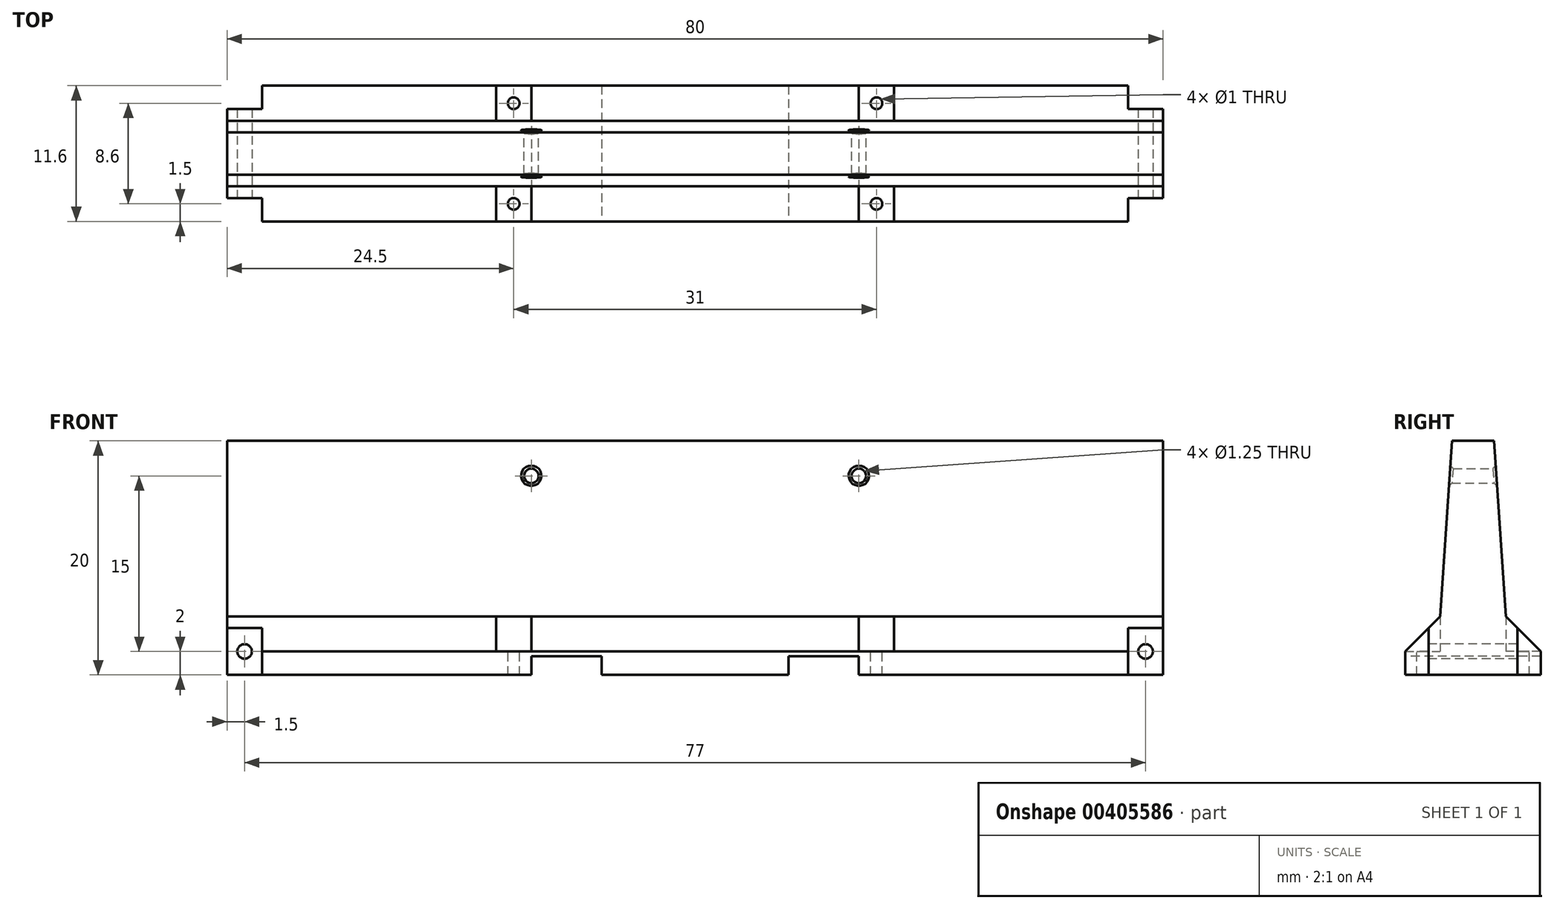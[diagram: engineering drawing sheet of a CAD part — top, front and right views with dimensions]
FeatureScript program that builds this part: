
annotation { "Feature Type Name" : "Feature", "Feature Type Description" : "" }
export const myFeature = defineFeature(function(context is Context, id is Id, definition is map)
    precondition{}
    {
        {
            var Q0;
            Q0=qCreatedBy(makeId("Top.planeOp"),FACE);
            var sketch = newSketch(context, id + "F0", { "sketchPlane" : qUnion([Q0])});
            skLineSegment(sketch, "E0.bottom", {"start": v(0, 0) * mm, "end": v(80, 0) * mm});
            skLineSegment(sketch, "E0.top", {"start": v(0, 11.6) * mm, "end": v(80, 11.6) * mm});
            skLineSegment(sketch, "E0.left", {"start": v(0, 0) * mm, "end": v(0, 11.6) * mm});
            skLineSegment(sketch, "E0.right", {"start": v(80, 0) * mm, "end": v(80, 11.6) * mm});
            skSolve(sketch);
        }
        {
            var Q0;
            Q0 = qSketchRegion(id + "F0", true);
            extrude(context, id + "F1", {"entities" : qUnion([Q0]), "depth" : 2 * mm});
        }
        {
            var Q0;
            Q0=makeQuery(id+"F1.opExtrude","SWEPT_FACE",FACE,{"disambiguationData":[OSD([sQuery(id+"F0.wireOp",EDGE,"E0.bottom")])]});
            var sketch = newSketch(context, id + "F2", { "sketchPlane" : qUnion([Q0])});
            skLineSegment(sketch, "E1", {"start": v(0, 0) * mm, "end": v(26, 0) * mm, "construction": true});
            skLineSegment(sketch, "E2", {"start": v(26, 0) * mm, "end": v(26, 1.6) * mm});
            skLineSegment(sketch, "E3", {"start": v(26, 1.6) * mm, "end": v(32, 1.6) * mm});
            skLineSegment(sketch, "E4", {"start": v(32, 1.6) * mm, "end": v(32, 0) * mm});
            skLineSegment(sketch, "E5", {"start": v(32, 0) * mm, "end": v(48, 0) * mm, "construction": true});
            skLineSegment(sketch, "E6", {"start": v(48, 0) * mm, "end": v(48, 1.6) * mm});
            skLineSegment(sketch, "E7", {"start": v(48, 1.6) * mm, "end": v(54, 1.6) * mm});
            skLineSegment(sketch, "E8", {"start": v(54, 1.6) * mm, "end": v(54, 0) * mm});
            skLineSegment(sketch, "E9", {"start": v(54, 0) * mm, "end": v(48, 0) * mm});
            skLineSegment(sketch, "E10", {"start": v(32, 0) * mm, "end": v(26, 0) * mm});
            skSolve(sketch);
        }
        {
            var Q0;
            Q0=makeQuery(id+"F2.imprint","IMPRINT",FACE,{"disambiguationData":[TD([[makeQuery(id+"F2.imprint","IMPRINT",EDGE,{"derivedFrom":sQuery(id+"F2.wireOp",EDGE,"E2")}),-1.0]])]});
            var Q1;
            Q1=makeQuery(id+"F2.imprint","IMPRINT",FACE,{"disambiguationData":[TD([[makeQuery(id+"F2.imprint","IMPRINT",EDGE,{"derivedFrom":sQuery(id+"F2.wireOp",EDGE,"E6")}),-1.0]])]});
            var Q2;
            Q2=sQuery(id+"F2.wireOp",EDGE,"E1");
            extrude(context, id + "F3", {"entities" : qUnion([Q0, Q1]), "operationType" : NewBodyOperationType.REMOVE, "surfaceEntities" : qUnion([Q2]), "oppositeDirection" : true, "depth" : 25 * mm});
        }
        {
            var Q0;
            Q0=makeQuery(id+"F1.opExtrude","CAP_FACE",FACE,{"disambiguationData":[OSD([sQuery(id+"F0.wireOp",EDGE,"E0.bottom"),sQuery(id+"F0.wireOp",EDGE,"E0.top"),sQuery(id+"F0.wireOp",EDGE,"E0.left"),sQuery(id+"F0.wireOp",EDGE,"E0.right")])],"isStart":false});
            var sketch = newSketch(context, id + "F4", { "sketchPlane" : qUnion([Q0])});
            skLineSegment(sketch, "E11.bottom", {"start": v(0, 11.6) * mm, "end": v(80, 11.6) * mm});
            skLineSegment(sketch, "E11.top", {"start": v(0, 0) * mm, "end": v(80, 0) * mm});
            skLineSegment(sketch, "E11.left", {"start": v(0, 11.6) * mm, "end": v(0, 0) * mm});
            skLineSegment(sketch, "E11.right", {"start": v(80, 11.6) * mm, "end": v(80, 0) * mm});
            skSolve(sketch);
        }
        {
            var Q0;
            Q0 = qSketchRegion(id + "F4", true);
            extrude(context, id + "F5", {"entities" : qUnion([Q0]), "operationType" : NewBodyOperationType.ADD, "depth" : 18 * mm});
        }
        {
            var Q0;
            Q0=makeQuery(id+"F5.boolean.opBoolean","MERGE",FACE,{"derivedFrom":[makeQuery(id+"F1.opExtrude","SWEPT_FACE",FACE,{"disambiguationData":[OSD([sQuery(id+"F0.wireOp",EDGE,"E0.right")])]}),makeQuery(id+"F5.opExtrude","SWEPT_FACE",FACE,{"disambiguationData":[OSD([sQuery(id+"F4.wireOp",EDGE,"E11.right")])]})]});
            var sketch = newSketch(context, id + "F6", { "sketchPlane" : qUnion([Q0])});
            skLineSegment(sketch, "E12", {"start": v(11.6, 0) * mm, "end": v(11.6, 2) * mm, "construction": true});
            skLineSegment(sketch, "E13", {"start": v(11.6, 2) * mm, "end": v(8.6, 5) * mm});
            skLineSegment(sketch, "E14", {"start": v(8.6, 5) * mm, "end": v(7.6, 20) * mm});
            skLineSegment(sketch, "E15", {"start": v(7.6, 20) * mm, "end": v(4, 20) * mm});
            skLineSegment(sketch, "E16", {"start": v(5.8, 0) * mm, "end": v(5.8, 20) * mm, "construction": true});
            skLineSegment(sketch, "E17.MirrorCS", {"start": v(3, 5) * mm, "end": v(4, 20) * mm});
            skLineSegment(sketch, "E18.MirrorCS", {"start": v(0, 2) * mm, "end": v(3, 5) * mm});
            skLineSegment(sketch, "E19", {"start": v(0, 2) * mm, "end": v(0, 0) * mm});
            skLineSegment(sketch, "E20", {"start": v(0, 0) * mm, "end": v(11.6, 0) * mm});
            skSolve(sketch);
        }
        {
            var Q0;
            {var subQ0=sQuery(id+"F6.wireOp",EDGE,"E17.MirrorCS");Q0=makeQuery(id+"F6.imprint","IMPRINT",FACE,{"disambiguationData":[TD([[makeQuery(id+"F6.imprint","IMPRINT",EDGE,{"derivedFrom":subQ0}),1.0]])]});}
            var Q1;
            {var subQ0=sQuery(id+"F6.wireOp",EDGE,"E13");Q1=makeQuery(id+"F6.imprint","IMPRINT",FACE,{"disambiguationData":[TD([[makeQuery(id+"F6.imprint","IMPRINT",EDGE,{"derivedFrom":subQ0}),-1.0]])]});}
            extrude(context, id + "F7", {"entities" : qUnion([Q0, Q1]), "operationType" : NewBodyOperationType.REMOVE, "oppositeDirection" : true, "depth" : 80 * mm});
        }
        {
            var Q0;
            {var subQ0=sQuery(id+"F0.wireOp",EDGE,"E0.bottom");var subQ1=sQuery(id+"F0.wireOp",EDGE,"E0.right");var subQ2=sQuery(id+"F0.wireOp",EDGE,"E0.top");Q0=makeQuery(id+"F3.boolean.opBoolean","SPLIT",FACE,{"disambiguationData":[TD([makeQuery(id+"F1.opExtrude","SWEPT_FACE",FACE,{"disambiguationData":[OSD([subQ1])]})])],"derivedFrom":makeQuery(id+"F1.opExtrude","CAP_FACE",FACE,{"disambiguationData":[OSD([subQ0,subQ2,sQuery(id+"F0.wireOp",EDGE,"E0.left"),subQ1])],"isStart":true})});}
            var sketch = newSketch(context, id + "F8", { "sketchPlane" : qUnion([Q0])});
            skLineSegment(sketch, "E21", {"start": v(0, 0) * mm, "end": v(26, 0) * mm, "construction": true});
            skLineSegment(sketch, "E22.bottom", {"start": v(26, 0) * mm, "end": v(23, 0) * mm});
            skLineSegment(sketch, "E22.top", {"start": v(26, -3) * mm, "end": v(23, -3) * mm});
            skLineSegment(sketch, "E22.left", {"start": v(26, 0) * mm, "end": v(26, -3) * mm});
            skLineSegment(sketch, "E22.right", {"start": v(23, 0) * mm, "end": v(23, -3) * mm});
            skLineSegment(sketch, "E23", {"start": v(0, 0) * mm, "end": v(0, -11.6) * mm, "construction": true});
            skLineSegment(sketch, "E24", {"start": v(0, -5.8) * mm, "end": v(7.98, -5.8) * mm, "construction": true});
            skLineSegment(sketch, "E25.MirrorCS", {"start": v(23, -11.6) * mm, "end": v(23, -8.6) * mm});
            skLineSegment(sketch, "E26.MirrorCS", {"start": v(0, -11.6) * mm, "end": v(26, -11.6) * mm, "construction": true});
            skLineSegment(sketch, "E27.MirrorCS", {"start": v(26, -11.6) * mm, "end": v(26, -8.6) * mm});
            skLineSegment(sketch, "E28.MirrorCS", {"start": v(26, -8.6) * mm, "end": v(23, -8.6) * mm});
            skLineSegment(sketch, "E29.bottom", {"start": v(23, -8.6) * mm, "end": v(26, -8.6) * mm});
            skLineSegment(sketch, "E29.top", {"start": v(23, -11.6) * mm, "end": v(26, -11.6) * mm});
            skLineSegment(sketch, "E29.left", {"start": v(23, -8.6) * mm, "end": v(23, -11.6) * mm});
            skLineSegment(sketch, "E29.right", {"start": v(26, -8.6) * mm, "end": v(26, -11.6) * mm});
            skLineSegment(sketch, "E30", {"start": v(0, 0) * mm, "end": v(40, 0) * mm, "construction": true});
            skLineSegment(sketch, "E31", {"start": v(40, 0) * mm, "end": v(40, -11.6) * mm, "construction": true});
            skLineSegment(sketch, "E32.MirrorCS", {"start": v(54, -3) * mm, "end": v(57, -3) * mm});
            skLineSegment(sketch, "E33.MirrorCS", {"start": v(57, 0) * mm, "end": v(57, -3) * mm});
            skLineSegment(sketch, "E34.MirrorCS", {"start": v(80, 0) * mm, "end": v(54, 0) * mm, "construction": true});
            skLineSegment(sketch, "E35.MirrorCS", {"start": v(54, 0) * mm, "end": v(54, -3) * mm});
            skLineSegment(sketch, "E36.MirrorCS", {"start": v(57, -8.6) * mm, "end": v(54, -8.6) * mm});
            skLineSegment(sketch, "E37.MirrorCS", {"start": v(57, -11.6) * mm, "end": v(57, -8.6) * mm});
            skLineSegment(sketch, "E38.MirrorCS", {"start": v(80, -11.6) * mm, "end": v(54, -11.6) * mm, "construction": true});
            skLineSegment(sketch, "E39.MirrorCS", {"start": v(54, -11.6) * mm, "end": v(54, -8.6) * mm});
            skLineSegment(sketch, "E40.bottom", {"start": v(54, 0) * mm, "end": v(57, 0) * mm});
            skLineSegment(sketch, "E41.bottom", {"start": v(54, -8.6) * mm, "end": v(57, -8.6) * mm});
            skLineSegment(sketch, "E41.top", {"start": v(54, -11.6) * mm, "end": v(57, -11.6) * mm});
            skLineSegment(sketch, "E41.left", {"start": v(54, -8.6) * mm, "end": v(54, -11.6) * mm});
            skLineSegment(sketch, "E41.right", {"start": v(57, -8.6) * mm, "end": v(57, -11.6) * mm});
            skSolve(sketch);
        }
        {
            var Q0;
            Q0 = qSketchRegion(id + "F8", true);
            extrude(context, id + "F9", {"entities" : qUnion([Q0]), "operationType" : NewBodyOperationType.REMOVE, "oppositeDirection" : true, "depth" : 25 * mm, "hasSecondDirection" : true, "secondDirectionOppositeDirection" : true, "secondDirectionDepth" : 2 * mm});
        }
        {
            var Q0;
            Q0=makeQuery(id+"F9.boolean.opBoolean","COPY",FACE,{"derivedFrom":makeQuery(id+"F9.opExtrude","CAP_FACE",FACE,{"disambiguationData":[OSD([sQuery(id+"F8.wireOp",EDGE,"E22.bottom"),sQuery(id+"F8.wireOp",EDGE,"E22.top"),sQuery(id+"F8.wireOp",EDGE,"E22.left"),sQuery(id+"F8.wireOp",EDGE,"E22.right")])],"isStart":true})});
            var sketch = newSketch(context, id + "F10", { "sketchPlane" : qUnion([Q0])});
            skCircle(sketch, "E42", {"center": v(24.5, 1.5) * mm, "radius": 0.5 * mm});
            skPoint(sketch, "E42.centerSnap0", {"position": v(24.5, 3) * mm});
            skPoint(sketch, "E42.centerSnap1", {"position": v(26, 1.5) * mm});
            skSolve(sketch);
        }
        {
            var Q0;
            Q0 = qSketchRegion(id + "F10", true);
            extrude(context, id + "F11", {"entities" : qUnion([Q0]), "operationType" : NewBodyOperationType.REMOVE, "oppositeDirection" : true, "depth" : 25 * mm});
        }
        {
            var Q0;
            Q0=makeQuery(id+"F9.boolean.opBoolean","COPY",FACE,{"derivedFrom":makeQuery(id+"F9.opExtrude","CAP_FACE",FACE,{"disambiguationData":[OSD([sQuery(id+"F8.wireOp",EDGE,"E29.bottom"),sQuery(id+"F8.wireOp",EDGE,"E29.top"),sQuery(id+"F8.wireOp",EDGE,"E29.left"),sQuery(id+"F8.wireOp",EDGE,"E29.right")])],"isStart":true})});
            var sketch = newSketch(context, id + "F12", { "sketchPlane" : qUnion([Q0])});
            skCircle(sketch, "E43", {"center": v(24.5, 10.1) * mm, "radius": 0.5 * mm});
            skPoint(sketch, "E43.centerSnap0", {"position": v(23, 10.1) * mm});
            skPoint(sketch, "E43.centerSnap1", {"position": v(24.5, 11.6) * mm});
            skSolve(sketch);
        }
        {
            var Q0;
            Q0 = qSketchRegion(id + "F12", true);
            extrude(context, id + "F13", {"entities" : qUnion([Q0]), "operationType" : NewBodyOperationType.REMOVE, "oppositeDirection" : true, "depth" : 25 * mm});
        }
        {
            var Q0;
            Q0=makeQuery(id+"F9.boolean.opBoolean","COPY",FACE,{"derivedFrom":makeQuery(id+"F9.opExtrude","CAP_FACE",FACE,{"disambiguationData":[OSD([sQuery(id+"F8.wireOp",EDGE,"E41.bottom"),sQuery(id+"F8.wireOp",EDGE,"E41.top"),sQuery(id+"F8.wireOp",EDGE,"E41.left"),sQuery(id+"F8.wireOp",EDGE,"E41.right")])],"isStart":true})});
            var sketch = newSketch(context, id + "F14", { "sketchPlane" : qUnion([Q0])});
            skCircle(sketch, "E44", {"center": v(55.5, 10.1) * mm, "radius": 0.5 * mm});
            skPoint(sketch, "E44.centerSnap0", {"position": v(54, 10.1) * mm});
            skPoint(sketch, "E44.centerSnap1", {"position": v(55.5, 11.6) * mm});
            skSolve(sketch);
        }
        {
            var Q0;
            Q0 = qSketchRegion(id + "F14", true);
            extrude(context, id + "F15", {"entities" : qUnion([Q0]), "operationType" : NewBodyOperationType.REMOVE, "oppositeDirection" : true, "depth" : 25 * mm});
        }
        {
            var Q0;
            Q0=makeQuery(id+"F9.boolean.opBoolean","COPY",FACE,{"derivedFrom":makeQuery(id+"F9.opExtrude","CAP_FACE",FACE,{"disambiguationData":[OSD([sQuery(id+"F8.wireOp",EDGE,"E40.bottom"),sQuery(id+"F8.wireOp",EDGE,"E32.MirrorCS"),sQuery(id+"F8.wireOp",EDGE,"E35.MirrorCS"),sQuery(id+"F8.wireOp",EDGE,"E33.MirrorCS")])],"isStart":true})});
            var sketch = newSketch(context, id + "F16", { "sketchPlane" : qUnion([Q0])});
            skCircle(sketch, "E45", {"center": v(55.5, 1.5) * mm, "radius": 0.5 * mm});
            skPoint(sketch, "E45.centerSnap0", {"position": v(54, 1.5) * mm});
            skPoint(sketch, "E45.centerSnap1", {"position": v(55.5, 0) * mm});
            skSolve(sketch);
        }
        {
            var Q0;
            Q0 = qSketchRegion(id + "F16", true);
            extrude(context, id + "F17", {"entities" : qUnion([Q0]), "operationType" : NewBodyOperationType.REMOVE, "oppositeDirection" : true, "depth" : 25 * mm});
        }
        {
            var Q0;
            Q0=makeQuery(id+"F5.boolean.opBoolean","MERGE",FACE,{"derivedFrom":[makeQuery(id+"F1.opExtrude","SWEPT_FACE",FACE,{"disambiguationData":[OSD([sQuery(id+"F0.wireOp",EDGE,"E0.bottom")])]}),makeQuery(id+"F5.opExtrude","SWEPT_FACE",FACE,{"disambiguationData":[OSD([sQuery(id+"F4.wireOp",EDGE,"E11.top")])]})]});
            var sketch = newSketch(context, id + "F18", { "sketchPlane" : qUnion([Q0])});
            skLineSegment(sketch, "E46.bottom", {"start": v(0, 0) * mm, "end": v(3, 0) * mm});
            skLineSegment(sketch, "E46.top", {"start": v(0, 5) * mm, "end": v(3, 5) * mm});
            skLineSegment(sketch, "E46.left", {"start": v(0, 0) * mm, "end": v(0, 5) * mm});
            skLineSegment(sketch, "E46.right", {"start": v(3, 0) * mm, "end": v(3, 5) * mm});
            skLineSegment(sketch, "E47.bottom", {"start": v(80, 0) * mm, "end": v(77, 0) * mm});
            skLineSegment(sketch, "E47.top", {"start": v(80, 5) * mm, "end": v(77, 5) * mm});
            skLineSegment(sketch, "E47.left", {"start": v(80, 0) * mm, "end": v(80, 5) * mm});
            skLineSegment(sketch, "E47.right", {"start": v(77, 0) * mm, "end": v(77, 5) * mm});
            skSolve(sketch);
        }
        {
            var Q0;
            Q0 = qSketchRegion(id + "F18", true);
            extrude(context, id + "F19", {"entities" : qUnion([Q0]), "operationType" : NewBodyOperationType.REMOVE, "oppositeDirection" : true, "depth" : 2 * mm});
        }
        {
            var Q0;
            Q0=makeQuery(id+"F5.boolean.opBoolean","MERGE",FACE,{"derivedFrom":[makeQuery(id+"F1.opExtrude","SWEPT_FACE",FACE,{"disambiguationData":[OSD([sQuery(id+"F0.wireOp",EDGE,"E0.top")])]}),makeQuery(id+"F5.opExtrude","SWEPT_FACE",FACE,{"disambiguationData":[OSD([sQuery(id+"F4.wireOp",EDGE,"E11.bottom")])]})]});
            var sketch = newSketch(context, id + "F20", { "sketchPlane" : qUnion([Q0])});
            skLineSegment(sketch, "E48.bottom", {"start": v(0, 0) * mm, "end": v(-3, 0) * mm});
            skLineSegment(sketch, "E48.top", {"start": v(0, 5.15) * mm, "end": v(-3, 5.15) * mm});
            skLineSegment(sketch, "E48.left", {"start": v(0, 0) * mm, "end": v(0, 5.15) * mm});
            skLineSegment(sketch, "E48.right", {"start": v(-3, 0) * mm, "end": v(-3, 5.15) * mm});
            skLineSegment(sketch, "E49.bottom", {"start": v(-80, 0) * mm, "end": v(-77, 0) * mm});
            skLineSegment(sketch, "E49.top", {"start": v(-80, 5) * mm, "end": v(-77, 5) * mm});
            skLineSegment(sketch, "E49.left", {"start": v(-80, 0) * mm, "end": v(-80, 5) * mm});
            skLineSegment(sketch, "E49.right", {"start": v(-77, 0) * mm, "end": v(-77, 5) * mm});
            skSolve(sketch);
        }
        {
            var Q0;
            Q0 = qSketchRegion(id + "F20", true);
            extrude(context, id + "F21", {"entities" : qUnion([Q0]), "operationType" : NewBodyOperationType.REMOVE, "oppositeDirection" : true, "depth" : 2 * mm});
        }
        {
            var Q0;
            Q0=makeQuery(id+"F19.boolean.opBoolean","COPY",FACE,{"derivedFrom":makeQuery(id+"F19.opExtrude","CAP_FACE",FACE,{"disambiguationData":[OSD([sQuery(id+"F18.wireOp",EDGE,"E46.bottom"),sQuery(id+"F18.wireOp",EDGE,"E46.top"),sQuery(id+"F18.wireOp",EDGE,"E46.left"),sQuery(id+"F18.wireOp",EDGE,"E46.right")])],"isStart":false})});
            var sketch = newSketch(context, id + "F22", { "sketchPlane" : qUnion([Q0])});
            skCircle(sketch, "E50", {"center": v(1.5, 2) * mm, "radius": 0.62 * mm});
            skPoint(sketch, "E50.centerSnap0", {"position": v(1.5, 0) * mm});
            skPoint(sketch, "E50.centerSnap1", {"position": v(0, 2) * mm});
            skSolve(sketch);
        }
        {
            var Q0;
            Q0 = qSketchRegion(id + "F22", true);
            extrude(context, id + "F23", {"entities" : qUnion([Q0]), "operationType" : NewBodyOperationType.REMOVE, "oppositeDirection" : true, "depth" : 25 * mm});
        }
        {
            var Q0;
            Q0=makeQuery(id+"F19.boolean.opBoolean","COPY",FACE,{"derivedFrom":makeQuery(id+"F19.opExtrude","CAP_FACE",FACE,{"disambiguationData":[OSD([sQuery(id+"F18.wireOp",EDGE,"E47.bottom"),sQuery(id+"F18.wireOp",EDGE,"E47.top"),sQuery(id+"F18.wireOp",EDGE,"E47.left"),sQuery(id+"F18.wireOp",EDGE,"E47.right")])],"isStart":false})});
            var sketch = newSketch(context, id + "F24", { "sketchPlane" : qUnion([Q0])});
            skCircle(sketch, "E51", {"center": v(78.5, 2) * mm, "radius": 0.62 * mm});
            skPoint(sketch, "E51.centerSnap0", {"position": v(80, 2) * mm});
            skPoint(sketch, "E51.centerSnap1", {"position": v(78.5, 0) * mm});
            skPoint(sketch, "E51.perimeterSnap0", {"position": v(80, 2) * mm});
            skSolve(sketch);
        }
        {
            var Q0;
            Q0 = qSketchRegion(id + "F24", true);
            extrude(context, id + "F25", {"entities" : qUnion([Q0]), "operationType" : NewBodyOperationType.REMOVE, "oppositeDirection" : true, "depth" : 25 * mm});
        }
        {
            var Q0;
            Q0=makeQuery(id+"F5.boolean.opBoolean","MERGE",FACE,{"derivedFrom":[makeQuery(id+"F1.opExtrude","SWEPT_FACE",FACE,{"disambiguationData":[OSD([sQuery(id+"F0.wireOp",EDGE,"E0.top")])]}),makeQuery(id+"F5.opExtrude","SWEPT_FACE",FACE,{"disambiguationData":[OSD([sQuery(id+"F4.wireOp",EDGE,"E11.bottom")])]})]});
            var sketch = newSketch(context, id + "F26", { "sketchPlane" : qUnion([Q0])});
            skLineSegment(sketch, "E52", {"start": v(-26, 1.6) * mm, "end": v(-26, 17) * mm, "construction": true});
            skLineSegment(sketch, "E53", {"start": v(-54, 1.6) * mm, "end": v(-54, 17) * mm, "construction": true});
            skCircle(sketch, "E54", {"center": v(-54, 17) * mm, "radius": 0.62 * mm});
            skCircle(sketch, "E55", {"center": v(-26, 17) * mm, "radius": 0.62 * mm});
            skSolve(sketch);
        }
        {
            var Q0;
            Q0 = qSketchRegion(id + "F26", true);
            extrude(context, id + "F27", {"entities" : qUnion([Q0]), "operationType" : NewBodyOperationType.REMOVE, "oppositeDirection" : true, "depth" : 25 * mm});
        }
        {
            var Q0;
            Q0=makeQuery(id+"F27.boolean.opBoolean","INTERSECT",EDGE,{"derivedFrom":[makeQuery(id+"F7.boolean.opBoolean","COPY",FACE,{"derivedFrom":makeQuery(id+"F7.opExtrude","SWEPT_FACE",FACE,{"disambiguationData":[OSD([sQuery(id+"F6.wireOp",EDGE,"E14")])]})}),makeQuery(id+"F27.opExtrude","SWEPT_FACE",FACE,{"disambiguationData":[OSD([sQuery(id+"F26.wireOp",EDGE,"E55")])]})]});
            var Q1;
            Q1=makeQuery(id+"F27.boolean.opBoolean","INTERSECT",EDGE,{"derivedFrom":[makeQuery(id+"F7.boolean.opBoolean","COPY",FACE,{"derivedFrom":makeQuery(id+"F7.opExtrude","SWEPT_FACE",FACE,{"disambiguationData":[OSD([sQuery(id+"F6.wireOp",EDGE,"E14")])]})}),makeQuery(id+"F27.opExtrude","SWEPT_FACE",FACE,{"disambiguationData":[OSD([sQuery(id+"F26.wireOp",EDGE,"E54")])]})]});
            var Q2;
            Q2=makeQuery(id+"F27.boolean.opBoolean","INTERSECT",EDGE,{"derivedFrom":[makeQuery(id+"F7.boolean.opBoolean","COPY",FACE,{"derivedFrom":makeQuery(id+"F7.opExtrude","SWEPT_FACE",FACE,{"disambiguationData":[OSD([sQuery(id+"F6.wireOp",EDGE,"E17.MirrorCS")])]})}),makeQuery(id+"F27.opExtrude","SWEPT_FACE",FACE,{"disambiguationData":[OSD([sQuery(id+"F26.wireOp",EDGE,"E55")])]})]});
            var Q3;
            Q3=makeQuery(id+"F27.boolean.opBoolean","INTERSECT",EDGE,{"derivedFrom":[makeQuery(id+"F7.boolean.opBoolean","COPY",FACE,{"derivedFrom":makeQuery(id+"F7.opExtrude","SWEPT_FACE",FACE,{"disambiguationData":[OSD([sQuery(id+"F6.wireOp",EDGE,"E17.MirrorCS")])]})}),makeQuery(id+"F27.opExtrude","SWEPT_FACE",FACE,{"disambiguationData":[OSD([sQuery(id+"F26.wireOp",EDGE,"E54")])]})]});
            chamfer(context, id + "F28", {"entities" : qUnion([Q0, Q1, Q2, Q3]), "width" : 0.25 * mm, "tangentPropagation" : true});
        }
    });
